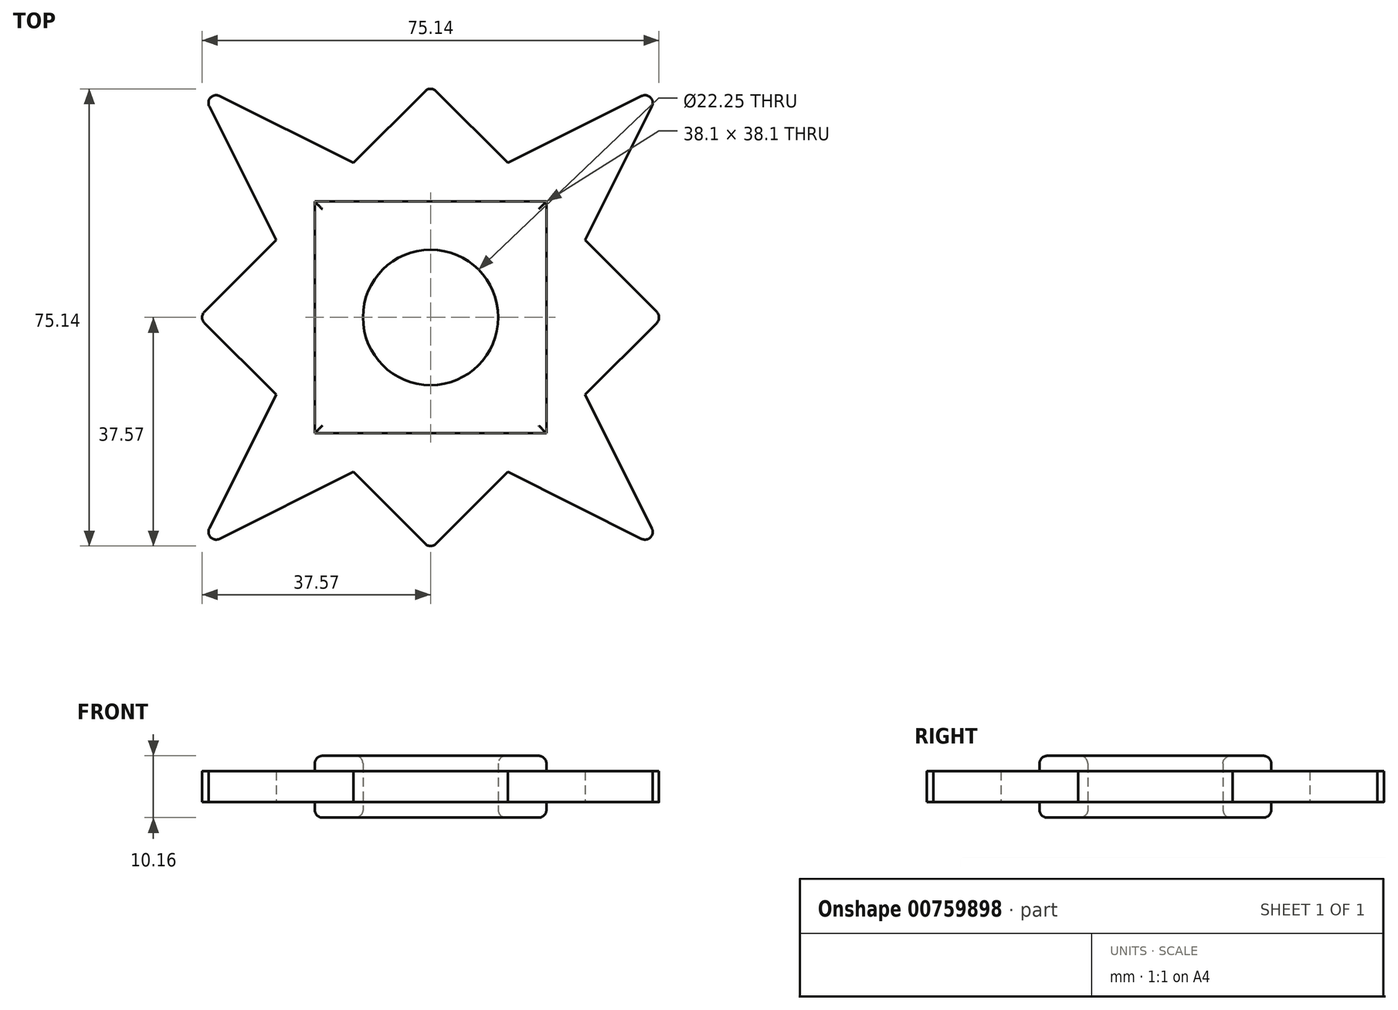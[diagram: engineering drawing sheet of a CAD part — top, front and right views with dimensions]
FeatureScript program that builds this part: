
annotation { "Feature Type Name" : "Feature", "Feature Type Description" : "" }
export const myFeature = defineFeature(function(context is Context, id is Id, definition is map)
    precondition{}
    {
        {
            var Q0;
            Q0=qCreatedBy(makeId("Top.planeOp"),FACE);
            var sketch = newSketch(context, id + "F0", { "sketchPlane" : qUnion([Q0])});
            skLineSegment(sketch, "E0.bottom", {"start": v(-19.05, 19.05) * mm, "end": v(19.05, 19.05) * mm});
            skLineSegment(sketch, "E0.top", {"start": v(-19.05, -19.05) * mm, "end": v(19.05, -19.05) * mm});
            skLineSegment(sketch, "E0.left", {"start": v(-19.05, 19.05) * mm, "end": v(-19.05, -19.05) * mm});
            skLineSegment(sketch, "E0.right", {"start": v(19.05, 19.05) * mm, "end": v(19.05, -19.05) * mm});
            skPoint(sketch, "E0.middle", {"position": v(0, 0) * mm});
            skCircle(sketch, "E1", {"center": v(0, 0) * mm, "radius": 11.13 * mm});
            skLineSegment(sketch, "E2", {"start": v(-19.05, -19.05) * mm, "end": v(0, -38.1) * mm});
            skLineSegment(sketch, "E3", {"start": v(0, -38.1) * mm, "end": v(19.05, -19.05) * mm});
            skLineSegment(sketch, "E4", {"start": v(-38.1, -38.1) * mm, "end": v(-12.7, -25.4) * mm});
            skLineSegment(sketch, "E5", {"start": v(38.1, -38.1) * mm, "end": v(12.7, -25.4) * mm});
            skLineSegment(sketch, "E6", {"start": v(19.05, 0) * mm, "end": v(-19.05, 0) * mm});
            skLineSegment(sketch, "E7.MirrorCS", {"start": v(-19.05, 19.05) * mm, "end": v(0, 38.1) * mm});
            skLineSegment(sketch, "E8.MirrorCS", {"start": v(0, 38.1) * mm, "end": v(19.05, 19.05) * mm});
            skLineSegment(sketch, "E9", {"start": v(-38.1, 38.1) * mm, "end": v(-12.7, 25.4) * mm});
            skLineSegment(sketch, "E10", {"start": v(38.1, 38.1) * mm, "end": v(12.7, 25.4) * mm});
            skLineSegment(sketch, "E11", {"start": v(19.05, -19.05) * mm, "end": v(38.1, 0) * mm});
            skLineSegment(sketch, "E12", {"start": v(38.1, 0) * mm, "end": v(19.05, 19.05) * mm});
            skLineSegment(sketch, "E13", {"start": v(25.4, 12.7) * mm, "end": v(38.1, 38.1) * mm});
            skLineSegment(sketch, "E14", {"start": v(25.4, -12.7) * mm, "end": v(38.1, -38.1) * mm});
            skLineSegment(sketch, "E15", {"start": v(38.1, 0) * mm, "end": v(-19.05, 0) * mm});
            skLineSegment(sketch, "E16.MirrorCS", {"start": v(-19.05, -19.05) * mm, "end": v(-38.1, 0) * mm});
            skLineSegment(sketch, "E17.MirrorCS", {"start": v(-38.1, 0) * mm, "end": v(-19.05, 19.05) * mm});
            skLineSegment(sketch, "E18", {"start": v(-25.4, -12.7) * mm, "end": v(-38.1, -38.1) * mm});
            skLineSegment(sketch, "E19", {"start": v(-25.4, 12.7) * mm, "end": v(-38.1, 38.1) * mm});
            skSolve(sketch);
        }
        {
            var Q0;
            {var subQ1=sQuery(id+"F0.wireOp",EDGE,"E0.top");var subQ11=sQuery(id+"F0.wireOp",EDGE,"E0.bottom");Q0=qUnion([makeQuery(id+"F0.imprint","IMPRINT",FACE,{"disambiguationData":[TD([[makeQuery(id+"F0.imprint","IMPRINT",EDGE,{"derivedFrom":subQ11}),-1.0]])]}),makeQuery(id+"F0.imprint","IMPRINT",FACE,{"disambiguationData":[TD([[makeQuery(id+"F0.imprint","IMPRINT",EDGE,{"derivedFrom":subQ1}),1.0]])]})]);}
            extrude(context, id + "F1", {"entities" : qUnion([Q0]), "endBound" : BoundingType.SYMMETRIC, "depth" : 10.16 * mm, "offsetDistance" : 25.4 * mm});
        }
        {
            var Q0;
            Q0=makeQuery(id+"F1.opExtrude","CAP_EDGE",EDGE,{"disambiguationData":[OSD([sQuery(id+"F0.wireOp",EDGE,"E0.right")])],"isStart":false});
            var Q1;
            Q1=makeQuery(id+"F1.opExtrude","CAP_EDGE",EDGE,{"disambiguationData":[OSD([sQuery(id+"F0.wireOp",EDGE,"E0.top")])],"isStart":false});
            var Q2;
            Q2=makeQuery(id+"F1.opExtrude","CAP_EDGE",EDGE,{"disambiguationData":[OSD([sQuery(id+"F0.wireOp",EDGE,"E0.left")])],"isStart":false});
            var Q3;
            Q3=makeQuery(id+"F1.opExtrude","CAP_EDGE",EDGE,{"disambiguationData":[OSD([sQuery(id+"F0.wireOp",EDGE,"E0.bottom")])],"isStart":false});
            var Q4;
            Q4=makeQuery(id+"F1.opExtrude","CAP_EDGE",EDGE,{"disambiguationData":[OSD([sQuery(id+"F0.wireOp",EDGE,"E1")])],"isStart":false});
            var Q5;
            Q5=makeQuery(id+"F1.opExtrude","CAP_EDGE",EDGE,{"disambiguationData":[OSD([sQuery(id+"F0.wireOp",EDGE,"E1")])],"isStart":true});
            var Q6;
            Q6=makeQuery(id+"F1.opExtrude","CAP_EDGE",EDGE,{"disambiguationData":[OSD([sQuery(id+"F0.wireOp",EDGE,"E0.right")])],"isStart":true});
            var Q7;
            Q7=makeQuery(id+"F1.opExtrude","CAP_EDGE",EDGE,{"disambiguationData":[OSD([sQuery(id+"F0.wireOp",EDGE,"E0.top")])],"isStart":true});
            var Q8;
            Q8=makeQuery(id+"F1.opExtrude","CAP_EDGE",EDGE,{"disambiguationData":[OSD([sQuery(id+"F0.wireOp",EDGE,"E0.bottom")])],"isStart":true});
            var Q9;
            Q9=makeQuery(id+"F1.opExtrude","CAP_EDGE",EDGE,{"disambiguationData":[OSD([sQuery(id+"F0.wireOp",EDGE,"E0.left")])],"isStart":true});
            fillet(context, id + "F2", {"entities" : qUnion([Q0, Q1, Q2, Q3, Q4, Q5, Q6, Q7, Q8, Q9]), "radius" : 1.27 * mm, "tangentPropagation" : true, "allowEdgeOverflow" : false});
        }
        {
            var Q0;
            {var subQ3=sQuery(id+"F0.wireOp",EDGE,"E4");Q0=makeQuery(id+"F0.imprint","IMPRINT",FACE,{"disambiguationData":[TD([[makeQuery(id+"F0.imprint","IMPRINT",EDGE,{"derivedFrom":subQ3}),1.0]])]});}
            var Q1;
            {var subQ4=sQuery(id+"F0.wireOp",EDGE,"E0.top");Q1=makeQuery(id+"F0.imprint","IMPRINT",FACE,{"disambiguationData":[TD([[makeQuery(id+"F0.imprint","IMPRINT",EDGE,{"derivedFrom":subQ4}),-1.0]])]});}
            var Q2;
            {var subQ3=sQuery(id+"F0.wireOp",EDGE,"E5");Q2=makeQuery(id+"F0.imprint","IMPRINT",FACE,{"disambiguationData":[TD([[makeQuery(id+"F0.imprint","IMPRINT",EDGE,{"derivedFrom":subQ3}),-1.0]])]});}
            var Q3;
            {var subQ3=sQuery(id+"F0.wireOp",EDGE,"E15");Q3=makeQuery(id+"F0.imprint","IMPRINT",FACE,{"disambiguationData":[TD([[makeQuery(id+"F0.imprint","IMPRINT",EDGE,{"derivedFrom":subQ3}),1.0]])]});}
            var Q4;
            {var subQ3=sQuery(id+"F0.wireOp",EDGE,"E15");Q4=makeQuery(id+"F0.imprint","IMPRINT",FACE,{"disambiguationData":[TD([[makeQuery(id+"F0.imprint","IMPRINT",EDGE,{"derivedFrom":subQ3}),-1.0]])]});}
            var Q5;
            {var subQ4=sQuery(id+"F0.wireOp",EDGE,"E0.bottom");Q5=makeQuery(id+"F0.imprint","IMPRINT",FACE,{"disambiguationData":[TD([[makeQuery(id+"F0.imprint","IMPRINT",EDGE,{"derivedFrom":subQ4}),1.0]])]});}
            var Q6;
            {var subQ0=sQuery(id+"F0.wireOp",EDGE,"E16.MirrorCS");var subQ3=makeQuery(id+"F0.imprint","INTERSECT",VERTEX,{"derivedFrom":[subQ0,sQuery(id+"F0.wireOp",EDGE,"E18")]});Q6=makeQuery(id+"F0.imprint","IMPRINT",FACE,{"disambiguationData":[TD([[makeQuery(id+"F0.imprint","IMPRINT",EDGE,{"disambiguationData":[TD([[subQ3,-1.0]])],"derivedFrom":subQ0}),-1.0]])]});}
            var Q7;
            {var subQ3=sQuery(id+"F0.wireOp",EDGE,"E9");Q7=makeQuery(id+"F0.imprint","IMPRINT",FACE,{"disambiguationData":[TD([[makeQuery(id+"F0.imprint","IMPRINT",EDGE,{"derivedFrom":subQ3}),-1.0]])]});}
            var Q8;
            {var subQ3=sQuery(id+"F0.wireOp",EDGE,"E10");Q8=makeQuery(id+"F0.imprint","IMPRINT",FACE,{"disambiguationData":[TD([[makeQuery(id+"F0.imprint","IMPRINT",EDGE,{"derivedFrom":subQ3}),1.0]])]});}
            extrude(context, id + "F3", {"entities" : qUnion([Q0, Q1, Q2, Q3, Q4, Q5, Q6, Q7, Q8]), "operationType" : NewBodyOperationType.ADD, "endBound" : BoundingType.SYMMETRIC, "depth" : 5.08 * mm, "offsetDistance" : 25.4 * mm});
        }
        {
            var Q0;
            Q0=makeQuery(id+"F3.opExtrude","SWEPT_EDGE",EDGE,{"disambiguationData":[OSD([sQuery(id+"F0.wireOp",EDGE,"E4"),sQuery(id+"F0.wireOp",EDGE,"E18")])]});
            var Q1;
            Q1=makeQuery(id+"F3.opExtrude","SWEPT_EDGE",EDGE,{"disambiguationData":[OSD([sQuery(id+"F0.wireOp",EDGE,"E16.MirrorCS"),sQuery(id+"F0.wireOp",EDGE,"E17.MirrorCS")])]});
            var Q2;
            Q2=makeQuery(id+"F3.opExtrude","SWEPT_EDGE",EDGE,{"disambiguationData":[OSD([sQuery(id+"F0.wireOp",EDGE,"E9"),sQuery(id+"F0.wireOp",EDGE,"E19")])]});
            var Q3;
            Q3=makeQuery(id+"F3.opExtrude","SWEPT_EDGE",EDGE,{"disambiguationData":[OSD([sQuery(id+"F0.wireOp",EDGE,"E7.MirrorCS"),sQuery(id+"F0.wireOp",EDGE,"E8.MirrorCS")])]});
            var Q4;
            Q4=makeQuery(id+"F3.opExtrude","SWEPT_EDGE",EDGE,{"disambiguationData":[OSD([sQuery(id+"F0.wireOp",EDGE,"E10"),sQuery(id+"F0.wireOp",EDGE,"E13")])]});
            var Q5;
            Q5=makeQuery(id+"F3.opExtrude","SWEPT_EDGE",EDGE,{"disambiguationData":[OSD([sQuery(id+"F0.wireOp",EDGE,"E11"),sQuery(id+"F0.wireOp",EDGE,"E12"),sQuery(id+"F0.wireOp",EDGE,"E15")])]});
            var Q6;
            Q6=makeQuery(id+"F3.opExtrude","SWEPT_EDGE",EDGE,{"disambiguationData":[OSD([sQuery(id+"F0.wireOp",EDGE,"E5"),sQuery(id+"F0.wireOp",EDGE,"E14")])]});
            var Q7;
            Q7=makeQuery(id+"F3.opExtrude","SWEPT_EDGE",EDGE,{"disambiguationData":[OSD([sQuery(id+"F0.wireOp",EDGE,"E2"),sQuery(id+"F0.wireOp",EDGE,"E3")])]});
            fillet(context, id + "F4", {"entities" : qUnion([Q0, Q1, Q2, Q3, Q4, Q5, Q6, Q7]), "radius" : 1.27 * mm, "tangentPropagation" : true, "allowEdgeOverflow" : false});
        }
    });
